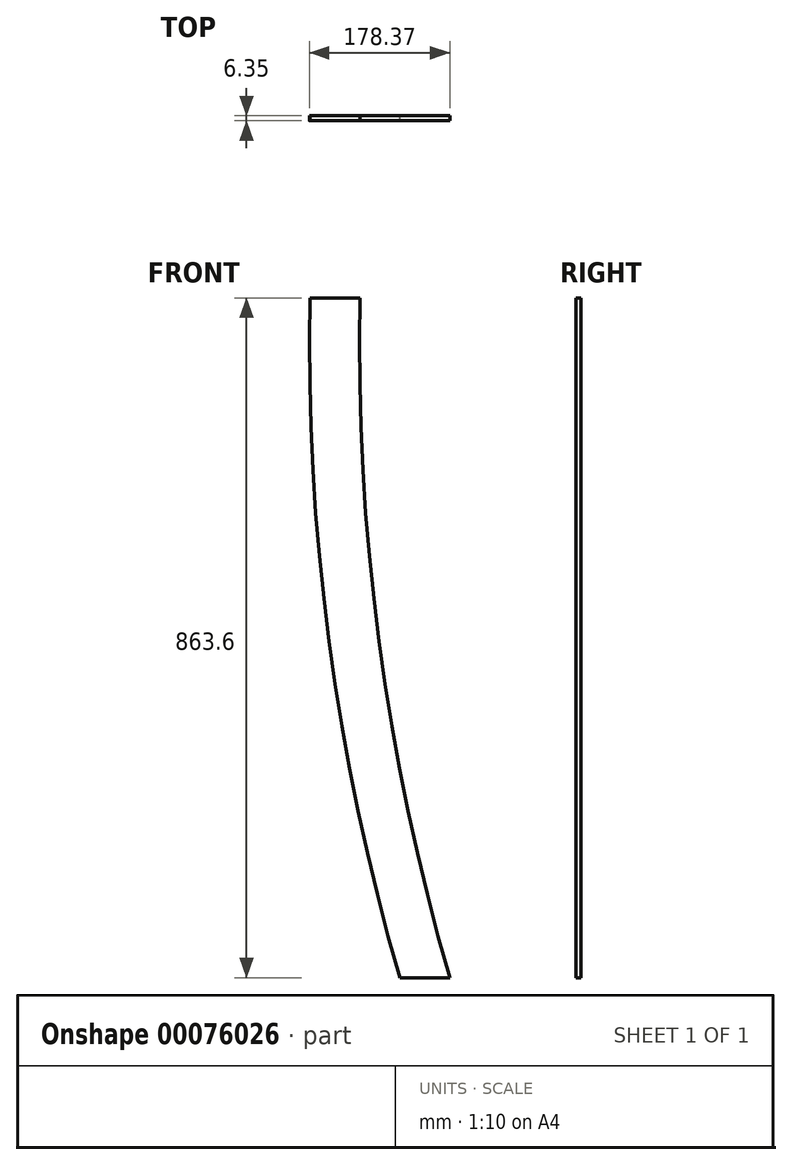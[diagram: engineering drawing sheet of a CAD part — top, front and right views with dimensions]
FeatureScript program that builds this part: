
annotation { "Feature Type Name" : "Feature", "Feature Type Description" : "" }
export const myFeature = defineFeature(function(context is Context, id is Id, definition is map)
    precondition{}
    {
        {
            var Q0;
            Q0=qCreatedBy(makeId("Front.planeOp"),FACE);
            var sketch = newSketch(context, id + "F0", { "sketchPlane" : qUnion([Q0])});
            skLineSegment(sketch, "E0", {"start": v(0, 0) * mm, "end": v(63.5, 0) * mm});
            skArc(sketch, "E1", {"start": v(-50.8, 863.6) * mm, "mid": v(-26.43, 427.46) * mm, "end": v(63.5, 0) * mm});
            skLineSegment(sketch, "E2", {"start": v(-50.8, 863.6) * mm, "end": v(-114.3, 863.6) * mm});
            skArc(sketch, "E3", {"start": v(-114.3, 863.6) * mm, "mid": v(-89.93, 427.46) * mm, "end": v(0, 0) * mm});
            skSolve(sketch);
        }
        {
            var Q0;
            Q0=makeQuery(id+"F0.imprint","IMPRINT",FACE,{"disambiguationData":[TD([[makeQuery(id+"F0.imprint","IMPRINT",EDGE,{"derivedFrom":sQuery(id+"F0.wireOp",EDGE,"E0")}),1.0]])]});
            extrude(context, id + "F1", {"entities" : qUnion([Q0]), "depth" : 6.35 * mm});
        }
    });
